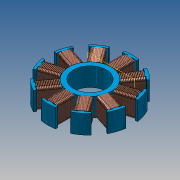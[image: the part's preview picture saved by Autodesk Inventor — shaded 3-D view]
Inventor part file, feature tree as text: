
AUTODESK INVENTOR PART (.ipt)
format: ipt  version: 2015 (Build 190159000, 159)  size: 2,128,384 bytes
history: native  units: mm
features: sketch x3, extrude x1, plane x1, sweep x1, pattern_linear x1, pattern_circular x1
ambient origin geometry x8: Origin, YZ Plane, XZ Plane, XY Plane, X Axis, Y Axis, Z Axis, Center Point
bodies: Solid1 (feature_tree)
feature tree (8):
  extrude  "Extrusion1"  Depth=2.0mm
  plane  "Work Plane1"
  sweep  "Sweep1"
  pattern_linear  "Rectangular Pattern1"  Spacing1=1.745329mm  [1 undecoded]
  pattern_circular  "Circular Pattern1"  [2 undecoded]
  sketch  "Sketch1"  dims[d0=14.0mm d1=2.0mm]
  sketch  "Sketch2"  dims[d2=18.0mm d3=1.0mm]
  sketch  "Sketch4"  dims[d4=1.0mm d6=1.745329mm d8=8.0mm d9=0.0mm d10=5.0mm d11=8.45mm d12=1.0mm d15=0.0mm d16=0.0mm d17=0.0mm d18=0.5mm d19=7.5mm d20=150.0mm d22=0.51mm d23=100.0mm d24=360.0deg]
note: 3 required parameter values undecoded (feature->parameter linkage not recoverable at this tier; creation-order binding heuristic only, values carry confidence <= 0.55)
